# Revit family: Lighting-Luminii-Kilo_Surface new
name_source: partatom
category: Lighting Fixtures
units: mm (PartAtom-declared; Revit-internal decimal feet)

## family parameters
Cut with Voids When Loaded = No
Host = Face
Light Source = Yes
OmniClass Number = 23.80.70.11.14.11
OmniClass Title = Downlights
Part Type = Normal
Room Calculation Point = No
Round Connector Dimension = Use Diameter
Shared = Yes

## types (1)
- Kilo Surface
    Apparent Load = 12 VA
    Assembly Code = D5040.50
    CCT = 3000K
    Color Filter = 16777215
    Constraints = 1
    Control Type = Consult Manufacturer Website for more Information
    Control Zone = Consult Manufacturer Website for more Information
    Current Amps = 50 A
    Default Elevation = 0"
    Description = Linear Illumination System
    Dimming Lamp Color Temperature Shift = <None>
    Dimming Type = Consult Manufacturer Website for more Information
    Emit from Line Length = 48"
    Environment = Indoor
    Finish = Metal - Luminii - Silver Anodized Aluminum
    Frequency = 60 Hz
    Has Battery Backup = No
    Has Dimming = Yes
    Height = 1 1/2"
    Housing Protection Rating = Consult Manufacturer Website for more Information
    Initial Color Comments = Perfomance based on 3000K Photometric Web File
    Keynote = 26 50 00
    Lamp = LED
    Lamp Life = 1
    Lens Material = Plastic - Luminii - Frosted Lens
    Load Classification = Lighting
    Luminaire Type = Linear Illumination System
    Manufacturer = Luminii
    Model = K
    Mounting Method = Mounting Options: Concealed Bracket, Adjustable Hinge Bracket
    Number of Poles = 1
    Operating Temperature = Consult Manufacturer Website for more Information
    Phase = 1
    Photometric Web File = KILO - CLEAR - LL72-VHO-30K_IES.IES
    Power Factor = 1
    Power Source Type = Driver
    Product Page URL = Consult Manufacturer Website for more Information
    Tilt Angle = -90.00°
    URL = https://www.luminii.com
    Version = 2020 - v1.0a
    Voltage = 120 V
    Voltage Comments = 120VAC - 277VAC
    Warranty URL = https://www.luminii.com
    Wattage Comments = 12 W/ft
    Width = 1 1/2"

## geometry (parser evidence)
native form markers: Sweep x4
no freeform markers — native parametric forms only
